# Revit family: VTi.901.I_Пресс_фитинг_Наруж резьба_Нерж_VALTEC
name_source: partatom
category: Соединительные детали трубопроводов
units: mm (PartAtom-declared; Revit-internal decimal feet)

## family parameters
Всегда вертикально = Да
На основе рабочей плоскости = Нет
Общий = Нет
При загрузке вырезать с полостями = Нет
Размер круглого соединителя = Использовать диаметр
Тип детали = Соединение

## types (7) — shared parameters
ADSK_Единица измерения = шт.
ADSK_Количество = 1
ADSK_Материал = Сталь, нержавеющая - VALTEC
LT = VTi.901.I_Пресс_фитинг_Наруж резьба_Нерж_VALTEC
zero-valued in all types: Отметка по умолчанию

## type names (no varying parameters)
- Пресс-фитинг из нержавеющей стали с наружной резьбой 12 мм х 1/2,12.00,15.00,14.50,13.38,20.90,5.00,8.00,8.50,0.60,5.00,5.90,15.00,2.40,24.23,0.05,VTi.901.I.001204
Пресс-фитинг из нержавеющей стали с наружной резьбой 15 мм х 1/2
- Пресс-фитинг из нержавеющей стали с наружной резьбой 15мм х 3/4,15.00,22.00,18.00,15.00,26.40,6.00,7.00,9.00,4.00,5.29,9.50,16.50,2.50,31.00,0.07,VTi.901.I.001505
Пресс-фитинг из нержавеющей стали с наружной резьбой 18 мм х 1/2
- Пресс-фитинг из нержавеющей стали с наружной резьбой 18 мм х 3/4,18.00,22.00,21.00,18.00,26.40,6.75,6.49,9.45,4.30,5.00,9.50,16.50,2.50,31.00,0.07,VTi.901.I.001805
Пресс-фитинг из нержавеющей стали с наружной резьбой 22 мм х 1/2
- Пресс-фитинг из нержавеющей стали с наружной резьбой 22 мм х 3/4,22.00,22.00,25.20,22.00,26.40,6.00,8.00,9.50,4.50,5.15,6.85,16.50,3.00,33.00,0.08,VTi.901.I.002205
Пресс-фитинг из нержавеющей стали с наружной резьбой 22 мм х 1
- Пресс-фитинг из нержавеющей стали с наружной резьбой 28 мм х 1,28.00,28.00,31.50,28.00,32.25,6.50,8.00,10.34,5.00,5.00,9.96,21.00,2.80,34.00,0.13,VTi.901.I.002806
Пресс-фитинг из нержавеющей стали с наружной резьбой 28 мм х 3/4
- Пресс-фитинг из нержавеющей стали с наружной резьбой 35 мм х 1,35.00,28.00,38.30,35.00,33.25,6.50,8.97,12.39,4.50,6.18,9.46,21.00,2.95,36.00,0.15,VTi.901.I.003506
Пресс-фитинг из нержавеющей стали с наружной резьбой 35 мм х 1 1/4
- Пресс-фитинг из нержавеющей стали с наружной резьбой 42 мм х 1 1/2,42.00,42.00,45.50,42.00,47.80,10.51,8.92,17.57,4.81,5.50,12.50,22.00,2.95,51.50,0.06,VTi.901.I.004208
Пресс-фитинг из нержавеющей стали с наружной резьбой 54мм х 2
